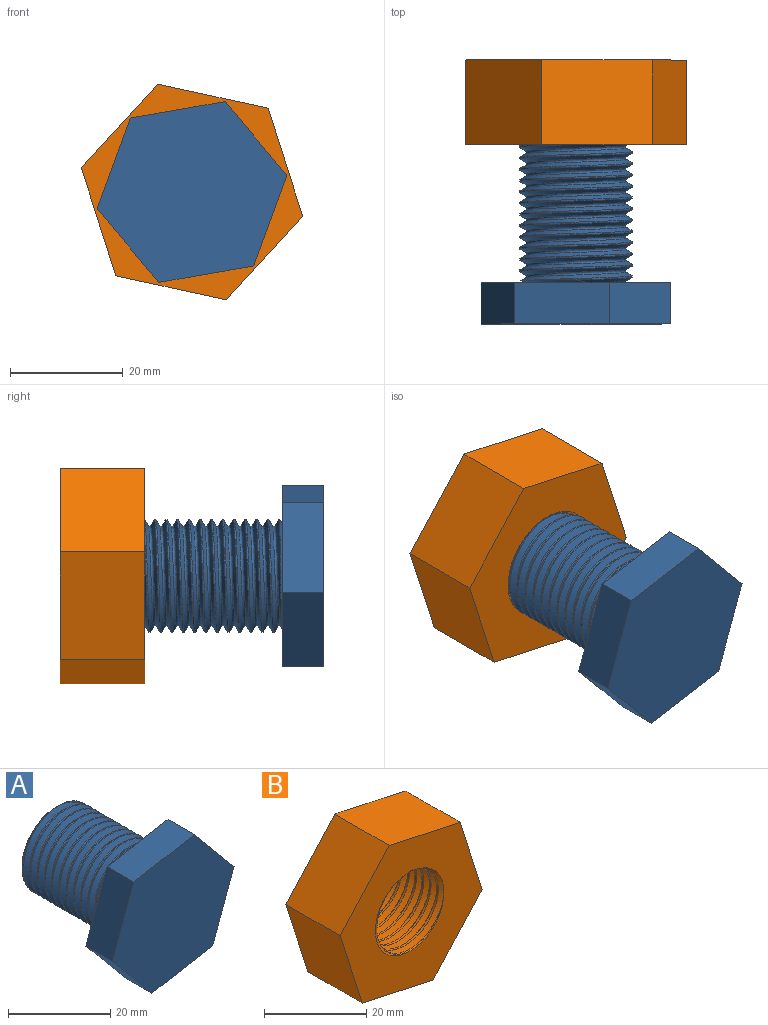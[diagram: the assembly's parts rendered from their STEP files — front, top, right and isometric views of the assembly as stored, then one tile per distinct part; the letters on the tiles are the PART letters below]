
ASSEMBLY  parts=2 mates=1
PART A: 16 faces, bbox 34.2x33.2x32.6 mm
  f0: cylinder r=10mm len=24mm, axis (0,1,0), area 293.9mm2, adj f10,f12,f13,f15
  f1: plane 19x19mm, normal (0,1,0), area 283.5mm2, adj f10
  f2: plane 13.11x10.95mm, normal (-0.77,0,-0.64), area 124.7mm2, adj f3,f7,f8,f9
  f3: plane 16.83x7.3mm, normal (0.17,0,-0.99), area 124.7mm2, adj f2,f4,f8,f9
  f4: plane 16.04x7.3mm, normal (0.94,0,-0.34), area 124.7mm2, adj f3,f5,f8,f9
  f5: plane 13.11x10.95mm, normal (0.77,0,0.64), area 124.7mm2, adj f4,f6,f8,f9
  f6: plane 16.83x7.3mm, normal (-0.17,0,0.99), area 124.7mm2, adj f5,f7,f8,f9
  f7: plane 16.04x7.3mm, normal (-0.94,0,0.34), area 124.7mm2, adj f2,f6,f8,f9
  f8: plane 33.66x32.08mm, normal (0,-1,0), area 758.2mm2, adj f2,f3,f4,f5,f6,f7
  f9: plane 33.78x32.2mm, normal (0,1,0), area 506mm2, adj f2,f3,f4,f5,f6,f7,f11,f12
  f10: cone r=10mm half-angle=45deg, axis (0,-1,0), area 43.3mm2, adj f0,f1,f14
  f11: bspline ~25.83x20.59mm, area 381.6mm2, adj f9,f12,f13,f14
  f12: bspline ~26.29x23.09mm, area 901.3mm2, adj f0,f9,f11,f14,f15
  f13: bspline ~25.29x23.09mm, area 900.8mm2, adj f0,f9,f11,f14,f15
  f14: plane 20.56x20.56mm, normal (0,-1,0), area 37.6mm2, adj f10,f11,f12,f13
  f15: cone r=10mm half-angle=63.4deg, axis (0,1,0), area 27.3mm2, adj f0,f9,f12,f13
PART B: 12 faces, bbox 39.8x18.4x38.9 mm
  f0: plane 19.62x15mm, normal (-0.21,0,-0.98), area 301.3mm2, adj f1,f5,f6,f7
  f1: plane 15x14.85mm, normal (0.74,0,-0.67), area 301.3mm2, adj f0,f2,f6,f7
  f2: plane 19.14x15mm, normal (0.95,0,0.3), area 301.3mm2, adj f1,f3,f6,f7
  f3: plane 19.62x15mm, normal (0.21,0,0.98), area 301.3mm2, adj f2,f4,f6,f7
  f4: plane 15x14.85mm, normal (-0.74,0,0.67), area 301.3mm2, adj f3,f5,f6,f7
  f5: plane 19.14x15mm, normal (-0.95,0,-0.3), area 301.3mm2, adj f0,f4,f6,f7
  f6: plane 39.41x38.44mm, normal (0,-1,0), area 765.2mm2, adj f0,f1,f2,f3,f4,f5,f8,f9
  f7: plane 39.83x38.87mm, normal (0,1,0), area 765.2mm2, adj f0,f1,f2,f3,f4,f5,f8,f9
  f8: bspline ~23.28x20.17mm, area 118.5mm2, adj f6,f7,f10,f11
  f9: bspline ~23.28x20.17mm, area 560.1mm2, adj f6,f7,f10,f11
  f10: bspline ~23.49x20.35mm, area 138.8mm2, adj f6,f7,f8,f9
  f11: cylinder r=9mm len=18mm, axis (0,-1,0), area 108.6mm2, adj f6,f7,f8,f9
PLACE A t=(-31.26,6.78,-18.1)mm
PLACE B t=(61.25,21.28,-21.83)mm
MATE revolute B.f11 <-> A.f0  axis (0,-1,0) through (10.55,6.28,19.98)mm
